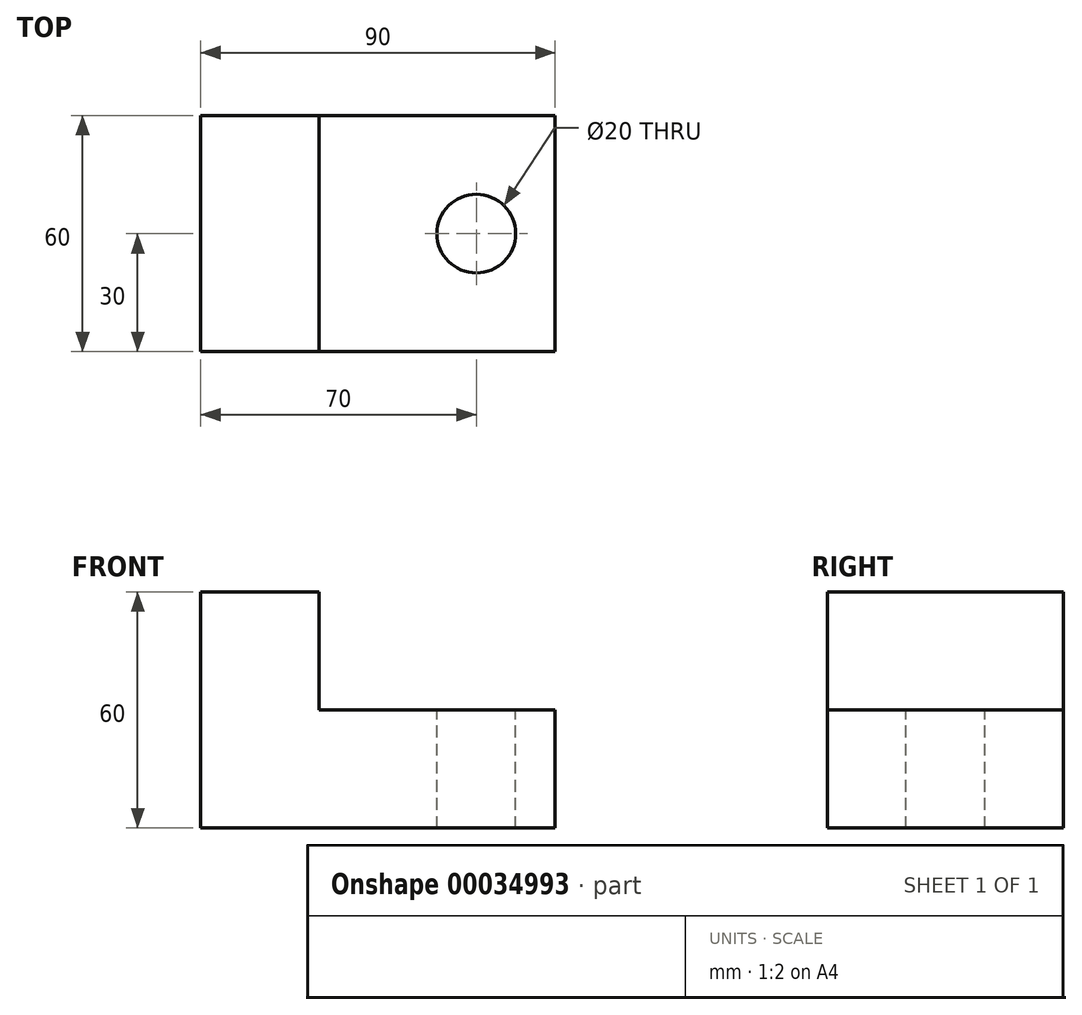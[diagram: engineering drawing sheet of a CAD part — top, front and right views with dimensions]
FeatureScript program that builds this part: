
annotation { "Feature Type Name" : "Feature", "Feature Type Description" : "" }
export const myFeature = defineFeature(function(context is Context, id is Id, definition is map)
    precondition{}
    {
        {
            var Q0;
            Q0=qCreatedBy(makeId("Front.planeOp"),FACE);
            var sketch = newSketch(context, id + "F0", { "sketchPlane" : qUnion([Q0])});
            skLineSegment(sketch, "E0.bottom", {"start": v(-41.13, 36.59) * mm, "end": v(48.87, 36.59) * mm});
            skLineSegment(sketch, "E0.top", {"start": v(-41.13, -23.41) * mm, "end": v(48.87, -23.41) * mm});
            skLineSegment(sketch, "E0.left", {"start": v(-41.13, 36.59) * mm, "end": v(-41.13, -23.41) * mm});
            skLineSegment(sketch, "E0.right", {"start": v(48.87, 36.59) * mm, "end": v(48.87, -23.41) * mm});
            skSolve(sketch);
        }
        {
            var Q0;
            Q0=makeQuery(id+"F0.imprint","IMPRINT",FACE,{"disambiguationData":[TD([[makeQuery(id+"F0.imprint","IMPRINT",EDGE,{"derivedFrom":sQuery(id+"F0.wireOp",EDGE,"E0.bottom")}),-1.0]])]});
            extrude(context, id + "F1", {"entities" : qUnion([Q0]), "depth" : 60 * mm});
        }
        {
            var Q0;
            Q0=makeQuery(id+"F1.opExtrude","SWEPT_FACE",FACE,{"disambiguationData":[OSD([sQuery(id+"F0.wireOp",EDGE,"E0.bottom")])]});
            var sketch = newSketch(context, id + "F2", { "sketchPlane" : qUnion([Q0])});
            skLineSegment(sketch, "E1.bottom", {"start": v(-11.13, 0) * mm, "end": v(48.87, 0) * mm});
            skLineSegment(sketch, "E1.top", {"start": v(-11.13, -60) * mm, "end": v(48.87, -60) * mm});
            skLineSegment(sketch, "E1.left", {"start": v(-11.13, 0) * mm, "end": v(-11.13, -60) * mm});
            skLineSegment(sketch, "E1.right", {"start": v(48.87, 0) * mm, "end": v(48.87, -60) * mm});
            skSolve(sketch);
        }
        {
            var Q0;
            Q0=makeQuery(id+"F2.imprint","IMPRINT",FACE,{"disambiguationData":[TD([[makeQuery(id+"F2.imprint","IMPRINT",EDGE,{"derivedFrom":sQuery(id+"F2.wireOp",EDGE,"E1.bottom")}),-1.0]])]});
            extrude(context, id + "F3", {"entities" : qUnion([Q0]), "operationType" : NewBodyOperationType.REMOVE, "oppositeDirection" : true, "depth" : 30 * mm});
        }
        {
            var Q0;
            Q0=makeQuery(id+"F3.boolean.opBoolean","COPY",FACE,{"derivedFrom":makeQuery(id+"F3.opExtrude","CAP_FACE",FACE,{"disambiguationData":[OSD([sQuery(id+"F2.wireOp",EDGE,"E1.bottom"),sQuery(id+"F2.wireOp",EDGE,"E1.top"),sQuery(id+"F2.wireOp",EDGE,"E1.left"),sQuery(id+"F2.wireOp",EDGE,"E1.right")])],"isStart":false})});
            var sketch = newSketch(context, id + "F4", { "sketchPlane" : qUnion([Q0])});
            skCircle(sketch, "E2", {"center": v(28.87, -30) * mm, "radius": 10 * mm});
            skSolve(sketch);
        }
        {
            var Q0;
            Q0=makeQuery(id+"F4.imprint","IMPRINT",FACE,{"disambiguationData":[TD([[makeQuery(id+"F4.imprint","IMPRINT",EDGE,{"derivedFrom":sQuery(id+"F4.wireOp",EDGE,"E2")}),1.0]])]});
            extrude(context, id + "F5", {"entities" : qUnion([Q0]), "operationType" : NewBodyOperationType.REMOVE, "oppositeDirection" : true, "depth" : 55.2 * mm});
        }
    });
